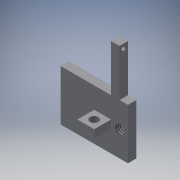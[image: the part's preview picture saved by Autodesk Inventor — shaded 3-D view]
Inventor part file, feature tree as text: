
AUTODESK INVENTOR PART (.ipt)
format: ipt  version: 2016 (Build 200138000, 138)  size: 137,216 bytes
history: native  units: in
note: dims shown in document units (in); Inventor stores cm internally (conversion verified against a paired STEP export)
features: sketch x6, hole x3, projected_geometry x3, extrude x2
ambient origin geometry x8: Origin, YZ Plane, XZ Plane, XY Plane, X Axis, Y Axis, Z Axis, Center Point
bodies: Solid1 (feature_tree)
feature tree (14):
  extrude  "Extrusion1"  Depth=1.0in
  extrude  "Extrusion2"  Depth=0.695in
  hole  "Hole1"  [1 undecoded]
  hole  "Hole2"  [1 undecoded]
  hole  "Hole3"  [1 undecoded]
  sketch  "Sketch6"  dims[d15=0.06in d16=0.75in d17=0.375in d18=0.25in d19=0.5635in d20=1.0in d21=0.8108in d22=0.125in d23=0.125in d24=0.75in d25=0.375in d26=0.25in d27=0.5635in d28=1.0in d29=0.8108in d30=0.13in d31=0.75in d32=0.375in d33=0.25in d34=0.5635in d35=1.0in d36=0.8108in d37=0.125in d38=0.063in]
  sketch  "Sketch1"  dims[d0=0.75in d2=1.0in]
  sketch  "Sketch2"  dims[d3=0.125in d4=0.695in]
  sketch  "Sketch3"  dims[d5=0.125in d6=0.0in d7=0.125in]
  projected_geometry  "Projected Loop1"
  sketch  "Sketch4"  dims[d10=0.25in d11=0.3125in]
  projected_geometry  "Projected Loop2"
  sketch  "Sketch5"  dims[d12=0.25in d13=0.25in d14=0.0in]
  projected_geometry  "Projected Loop3"
note: 3 required parameter values undecoded (feature->parameter linkage not recoverable at this tier; creation-order binding heuristic only, values carry confidence <= 0.55)
